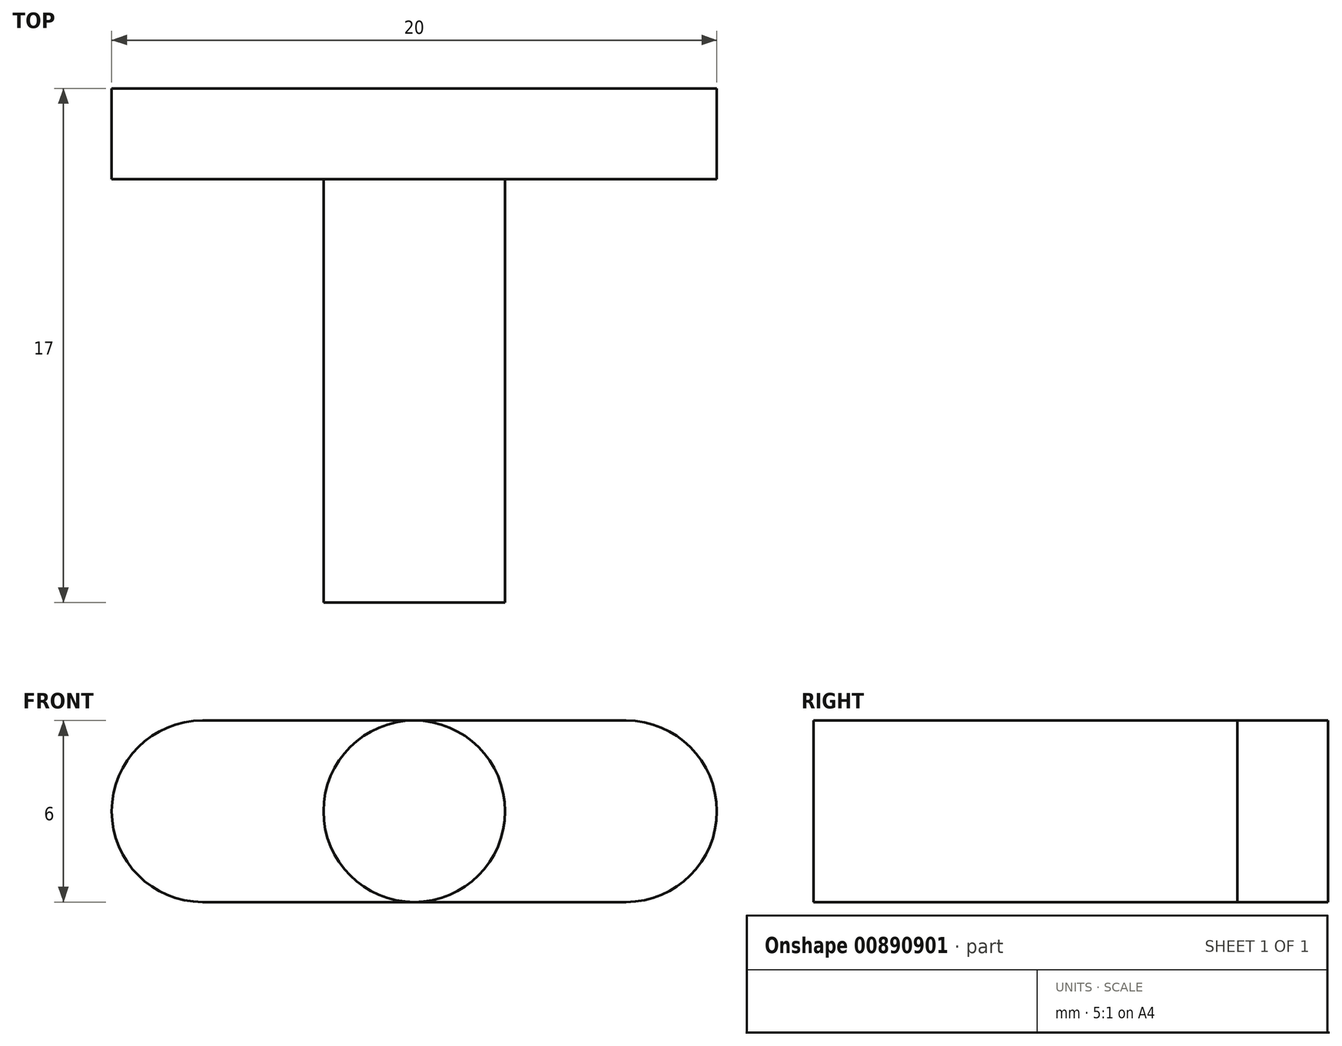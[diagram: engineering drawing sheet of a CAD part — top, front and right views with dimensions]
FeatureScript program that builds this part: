
annotation { "Feature Type Name" : "Feature", "Feature Type Description" : "" }
export const myFeature = defineFeature(function(context is Context, id is Id, definition is map)
    precondition{}
    {
        {
            var Q0;
            Q0=qCreatedBy(makeId("Front.planeOp"),FACE);
            var sketch = newSketch(context, id + "F0", { "sketchPlane" : qUnion([Q0])});
            skCircle(sketch, "E0", {"center": v(0, 0) * mm, "radius": 3 * mm});
            skSolve(sketch);
        }
        {
            var Q0;
            Q0 = qSketchRegion(id + "F0", true);
            extrude(context, id + "F1", {"entities" : qUnion([Q0]), "depth" : 14 * mm, "offsetDistance" : 25 * mm});
        }
        {
            var Q0;
            Q0=makeQuery(id+"F1.opExtrude","CAP_FACE",FACE,{"disambiguationData":[OSD([sQuery(id+"F0.wireOp",EDGE,"E0")])],"isStart":true});
            var sketch = newSketch(context, id + "F2", { "sketchPlane" : qUnion([Q0])});
            skLineSegment(sketch, "E1.bottom", {"start": v(-7, -3) * mm, "end": v(7, -3) * mm});
            skLineSegment(sketch, "E1.top", {"start": v(-7, 3) * mm, "end": v(7, 3) * mm});
            skLineSegment(sketch, "E1.left", {"start": v(-10, 0) * mm, "end": v(-10, 0) * mm});
            skLineSegment(sketch, "E1.right", {"start": v(10, 0) * mm, "end": v(10, 0) * mm});
            skPoint(sketch, "E1.middle", {"position": v(0, 0) * mm});
            skPoint(sketch, "E2.visualSharp", {"position": v(-10, 3) * mm});
            skArc(sketch, "E2.filletArc", {"start": v(-7, 3) * mm, "mid": v(-9.12, 2.12) * mm, "end": v(-10, 0) * mm});
            skPoint(sketch, "E3.visualSharp", {"position": v(-10, -3) * mm});
            skArc(sketch, "E3.filletArc", {"start": v(-10, 0) * mm, "mid": v(-9.12, -2.12) * mm, "end": v(-7, -3) * mm});
            skPoint(sketch, "E4.visualSharp", {"position": v(10, -3) * mm});
            skArc(sketch, "E4.filletArc", {"start": v(7, -3) * mm, "mid": v(9.12, -2.12) * mm, "end": v(10, 0) * mm});
            skPoint(sketch, "E5.visualSharp", {"position": v(10, 3) * mm});
            skArc(sketch, "E5.filletArc", {"start": v(10, 0) * mm, "mid": v(9.12, 2.12) * mm, "end": v(7, 3) * mm});
            skSolve(sketch);
        }
        {
            var Q0;
            {var subQ0=sQuery(id+"F2.wireOp",EDGE,"E2.filletArc");Q0=makeQuery(id+"F2.imprint","IMPRINT",FACE,{"disambiguationData":[TD([[makeQuery(id+"F2.imprint","IMPRINT",EDGE,{"derivedFrom":subQ0}),1.0]])]});}
            var Q1;
            {var subQ4=sQuery(id+"F2.wireOp",EDGE,"E4.filletArc");Q1=makeQuery(id+"F2.imprint","IMPRINT",FACE,{"disambiguationData":[TD([[makeQuery(id+"F2.imprint","IMPRINT",EDGE,{"derivedFrom":subQ4}),1.0]])]});}
            var Q2;
            {var subQ0=makeQuery(id+"F1.opExtrude","CAP_EDGE",EDGE,{"disambiguationData":[OSD([sQuery(id+"F0.wireOp",EDGE,"E0")])],"isStart":true});var subQ1=makeQuery(id+"F2.imprint","INTERSECT",VERTEX,{"derivedFrom":[subQ0,sQuery(id+"F2.wireOp",EDGE,"E1.bottom")]});Q2=makeQuery(id+"F2.imprint","IMPRINT",FACE,{"disambiguationData":[TD([[makeQuery(id+"F2.imprint","IMPRINT",EDGE,{"disambiguationData":[TD([[subQ1,-1.0]])],"derivedFrom":subQ0}),-1.0]])]});}
            extrude(context, id + "F3", {"entities" : qUnion([Q0, Q1, Q2]), "operationType" : NewBodyOperationType.ADD, "depth" : 3 * mm, "offsetDistance" : 25 * mm});
        }
    });
